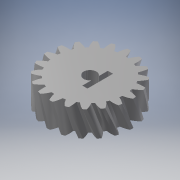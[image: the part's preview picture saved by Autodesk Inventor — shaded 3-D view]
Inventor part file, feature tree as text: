
AUTODESK INVENTOR PART (.ipt)
format: ipt  version: 2017 SP1 (Build 210196100, 196)  size: 439,296 bytes
history: native  units: mm (DEFAULTED — no unit token found)
features: plane x3, other x3, sketch x3, extrude x2
ambient origin geometry x8: Origin, YZ Plane, XZ Plane, XY Plane, X Axis, Y Axis, Z Axis, Center Point
bodies: Solid1 (feature_tree)
feature tree (11):
  extrude  "Extrusion1"  Depth=10.0mm TaperAngle=0.0deg
  plane  "Work Plane2"
  plane  "Work Plane8"
  plane  "Work Plane9"
  other  "Engrenage cylindrique"
  extrude  "Extrusion2"  Depth=10.0mm TaperAngle=0.0deg
  sketch  "Sketch1"  dims[d0=32.749068mm d1=10.0mm d2=0.0mm]
  sketch  "Sketch2"  dims[d3=30.066593mm d4=10.0mm d5=0.0mm d16=30.066593mm d17=0.0mm d34=1.570796mm d39=0.0mm d41=0.0mm d43=30.066593mm d46=30.066593mm d47=0.0mm d48=0.0mm d49=5.0mm d50=5.0mm d51=5.0mm d52=2.0mm d53=2.0mm d54=10.0mm d55=0.0mm]
  other  "Srf1"
  sketch  "Esquisse3"
  other  "Diamètre primitif"
